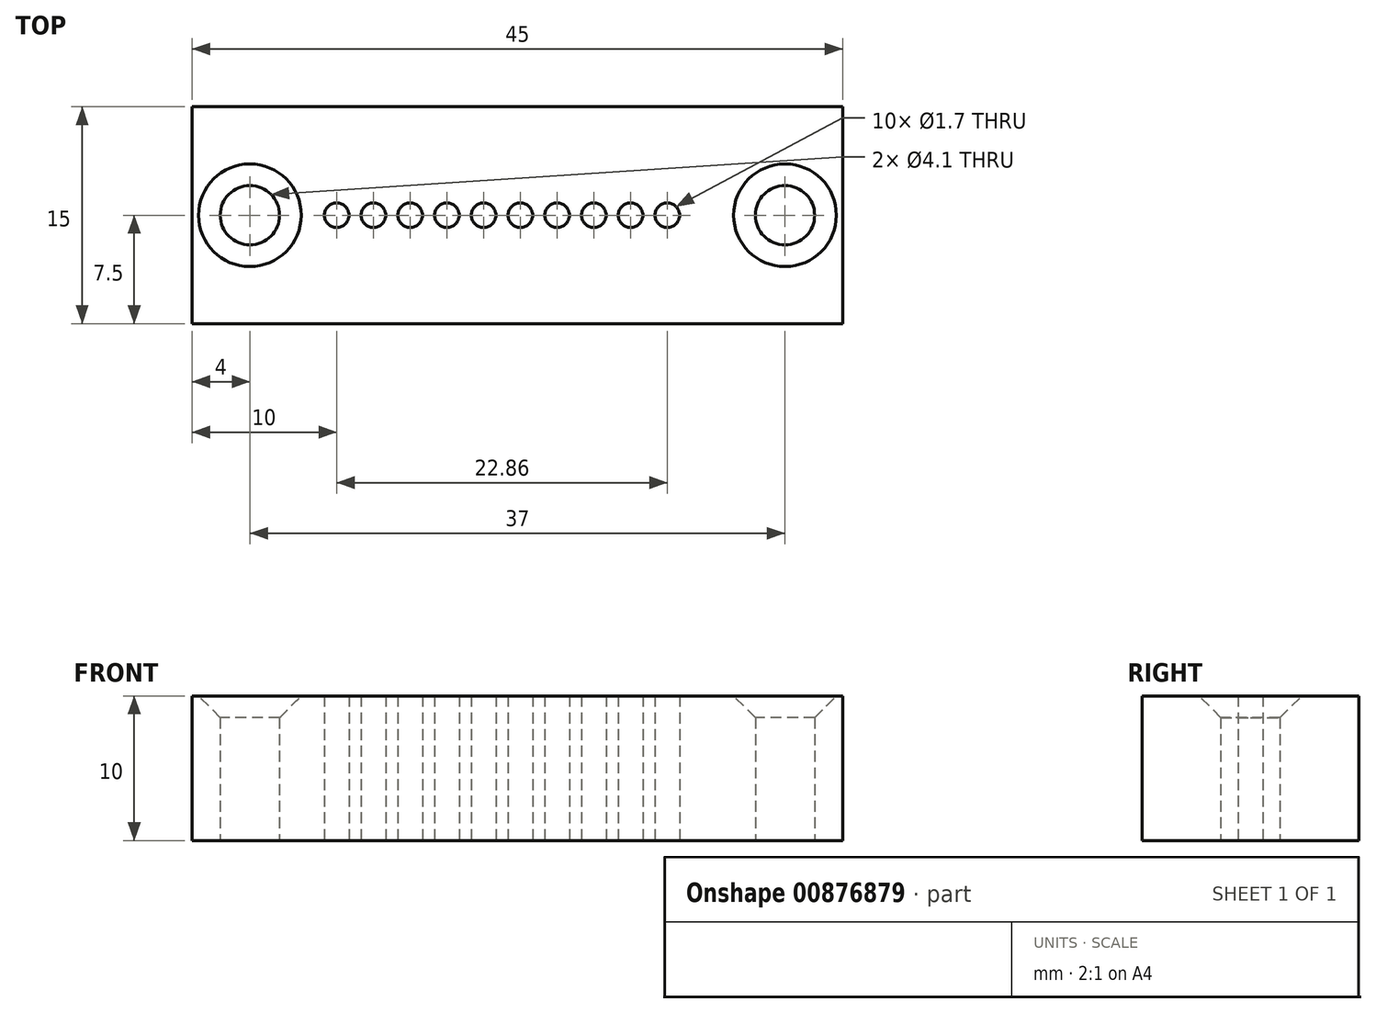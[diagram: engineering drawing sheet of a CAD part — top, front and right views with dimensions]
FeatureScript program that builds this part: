
annotation { "Feature Type Name" : "Feature", "Feature Type Description" : "" }
export const myFeature = defineFeature(function(context is Context, id is Id, definition is map)
    precondition{}
    {
        {
            var Q0;
            Q0=qCreatedBy(makeId("Top.planeOp"),FACE);
            var sketch = newSketch(context, id + "F0", { "sketchPlane" : qUnion([Q0])});
            skLineSegment(sketch, "E0.bottom", {"start": v(-10, 7.5) * mm, "end": v(35, 7.5) * mm});
            skLineSegment(sketch, "E0.top", {"start": v(-10, -7.5) * mm, "end": v(35, -7.5) * mm});
            skLineSegment(sketch, "E0.left", {"start": v(-10, 7.5) * mm, "end": v(-10, -7.5) * mm});
            skLineSegment(sketch, "E0.right", {"start": v(35, 7.5) * mm, "end": v(35, -7.5) * mm});
            skCircle(sketch, "E1", {"center": v(0, 0) * mm, "radius": 0.85 * mm});
            skCircle(sketch, "E2.1.0.0", {"center": v(2.54, 0) * mm, "radius": 0.85 * mm});
            skCircle(sketch, "E2.2.0.0", {"center": v(5.08, 0) * mm, "radius": 0.85 * mm});
            skCircle(sketch, "E2.3.0.0", {"center": v(7.62, 0) * mm, "radius": 0.85 * mm});
            skCircle(sketch, "E2.4.0.0", {"center": v(10.16, 0) * mm, "radius": 0.85 * mm});
            skCircle(sketch, "E2.5.0.0", {"center": v(12.7, 0) * mm, "radius": 0.85 * mm});
            skCircle(sketch, "E2.6.0.0", {"center": v(15.24, 0) * mm, "radius": 0.85 * mm});
            skCircle(sketch, "E2.7.0.0", {"center": v(17.78, 0) * mm, "radius": 0.85 * mm});
            skCircle(sketch, "E2.8.0.0", {"center": v(20.32, 0) * mm, "radius": 0.85 * mm});
            skCircle(sketch, "E2.9.0.0", {"center": v(22.86, 0) * mm, "radius": 0.85 * mm});
            skLineSegment(sketch, "E2.direction1", {"start": v(0, 0) * mm, "end": v(2.54, 0) * mm, "construction": true});
            skCircle(sketch, "E3", {"center": v(-6, 0) * mm, "radius": 2.05 * mm});
            skCircle(sketch, "E4", {"center": v(31, 0) * mm, "radius": 2.05 * mm});
            skSolve(sketch);
        }
        {
            var Q0;
            Q0 = qSketchRegion(id + "F0", true);
            extrude(context, id + "F1", {"entities" : qUnion([Q0]), "depth" : 10 * mm, "offsetDistance" : 25 * mm});
        }
        {
            var Q0;
            Q0=makeQuery(id+"F1.opExtrude","CAP_EDGE",EDGE,{"disambiguationData":[OSD([sQuery(id+"F0.wireOp",EDGE,"E3")])],"isStart":false});
            var Q1;
            Q1=makeQuery(id+"F1.opExtrude","CAP_EDGE",EDGE,{"disambiguationData":[OSD([sQuery(id+"F0.wireOp",EDGE,"E4")])],"isStart":false});
            chamfer(context, id + "F2", {"entities" : qUnion([Q0, Q1]), "width" : 1.5 * mm, "tangentPropagation" : true});
        }
    });
